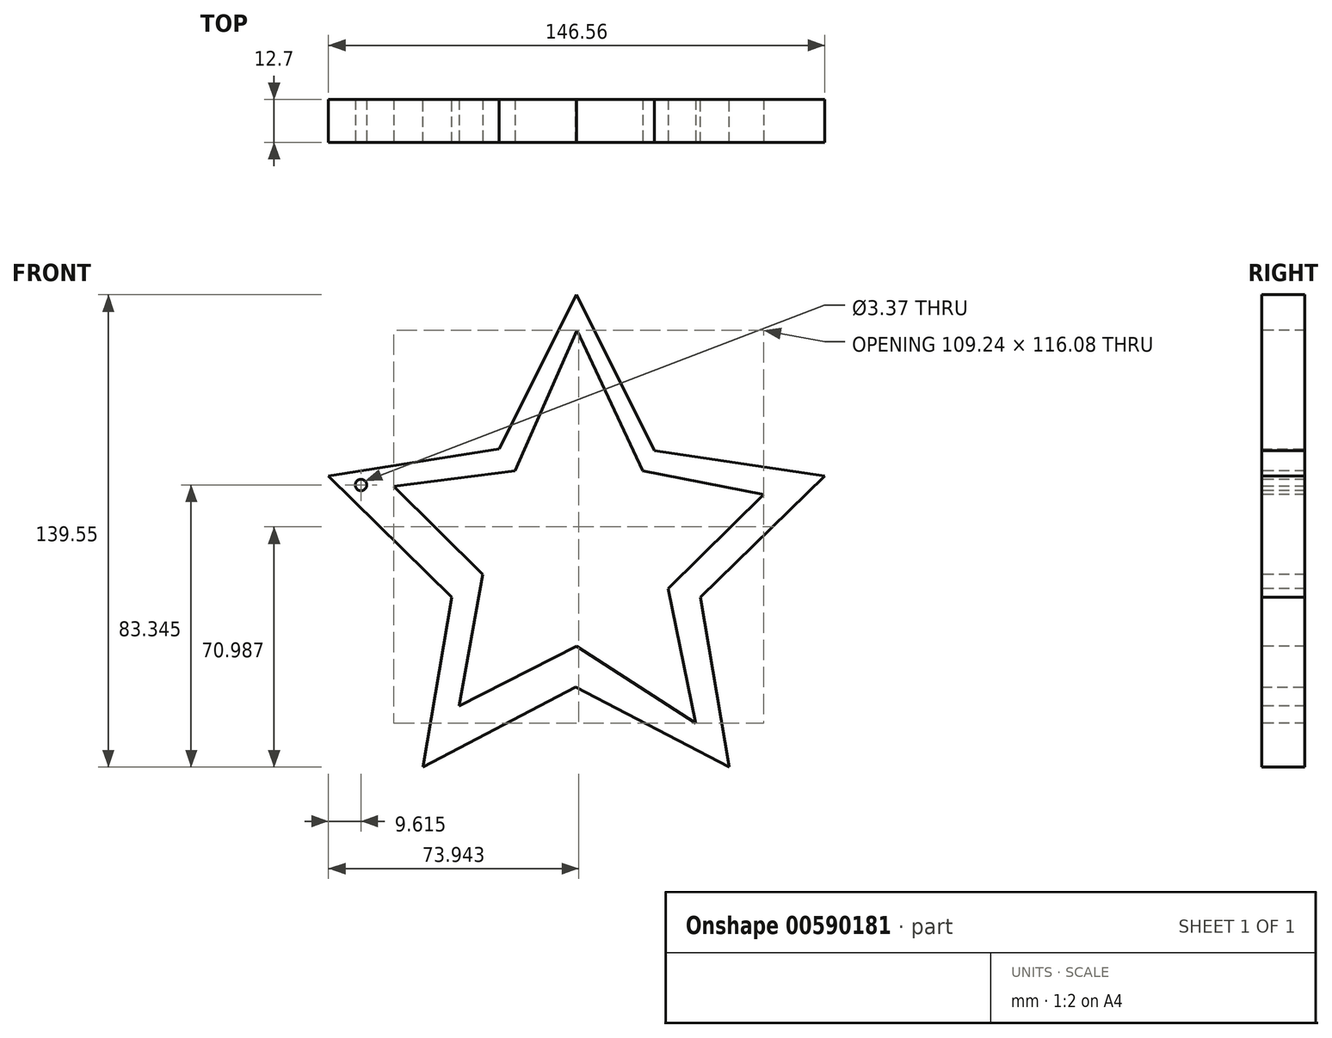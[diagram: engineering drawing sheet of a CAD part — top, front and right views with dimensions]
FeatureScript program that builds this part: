
annotation { "Feature Type Name" : "Feature", "Feature Type Description" : "" }
export const myFeature = defineFeature(function(context is Context, id is Id, definition is map)
    precondition{}
    {
        {
            var Q0;
            Q0=qCreatedBy(makeId("Front.planeOp"),FACE);
            var sketch = newSketch(context, id + "F0", { "sketchPlane" : qUnion([Q0])});
            skLineSegment(sketch, "E0", {"start": v(-16.38, 0) * mm, "end": v(-39.2, -45.54) * mm});
            skLineSegment(sketch, "E1", {"start": v(-39.2, -45.54) * mm, "end": v(-89.66, -53.55) * mm});
            skLineSegment(sketch, "E2", {"start": v(-89.66, -53.55) * mm, "end": v(-53.23, -89.36) * mm});
            skLineSegment(sketch, "E3", {"start": v(-53.23, -89.36) * mm, "end": v(-61.75, -139.55) * mm});
            skLineSegment(sketch, "E4", {"start": v(-61.75, -139.55) * mm, "end": v(-16.67, -115.9) * mm});
            skLineSegment(sketch, "E5", {"start": v(-16.67, -115.9) * mm, "end": v(28.66, -139.55) * mm});
            skLineSegment(sketch, "E6", {"start": v(28.66, -139.55) * mm, "end": v(20.14, -89.36) * mm});
            skLineSegment(sketch, "E7", {"start": v(20.14, -89.36) * mm, "end": v(56.9, -53.55) * mm});
            skLineSegment(sketch, "E8", {"start": v(56.9, -53.55) * mm, "end": v(6.62, -46.04) * mm});
            skLineSegment(sketch, "E9", {"start": v(6.62, -46.04) * mm, "end": v(-16.38, 0) * mm});
            skSolve(sketch);
        }
        {
            var Q0;
            Q0=qSketchRegion(id+"F0",true);
            extrude(context, id + "F1", {"entities" : qUnion([Q0]), "depth" : 12.7 * mm, "offsetDistance" : 25.4 * mm});
        }
        {
            var Q0;
            Q0=makeQuery(id+"F1.opExtrude","CAP_FACE",FACE,{"disambiguationData":[OSD([sQuery(id+"F0.wireOp",EDGE,"E0"),sQuery(id+"F0.wireOp",EDGE,"E1"),sQuery(id+"F0.wireOp",EDGE,"E2"),sQuery(id+"F0.wireOp",EDGE,"E3"),sQuery(id+"F0.wireOp",EDGE,"E4"),sQuery(id+"F0.wireOp",EDGE,"E5"),sQuery(id+"F0.wireOp",EDGE,"E6"),sQuery(id+"F0.wireOp",EDGE,"E7"),sQuery(id+"F0.wireOp",EDGE,"E8"),sQuery(id+"F0.wireOp",EDGE,"E9")])],"isStart":false});
            var sketch = newSketch(context, id + "F2", { "sketchPlane" : qUnion([Q0])});
            skLineSegment(sketch, "E10", {"start": v(-16.27, -10.52) * mm, "end": v(-34.59, -52.01) * mm});
            skLineSegment(sketch, "E11", {"start": v(-34.59, -52.01) * mm, "end": v(-70.34, -56.65) * mm});
            skLineSegment(sketch, "E12", {"start": v(-70.34, -56.65) * mm, "end": v(-44.07, -82.69) * mm});
            skLineSegment(sketch, "E13", {"start": v(-44.07, -82.69) * mm, "end": v(-51.14, -121.53) * mm});
            skLineSegment(sketch, "E14", {"start": v(-51.14, -121.53) * mm, "end": v(-16.38, -103.87) * mm});
            skLineSegment(sketch, "E15", {"start": v(-16.38, -103.87) * mm, "end": v(18.82, -126.6) * mm});
            skLineSegment(sketch, "E16", {"start": v(18.82, -126.6) * mm, "end": v(10.65, -86.88) * mm});
            skLineSegment(sketch, "E17", {"start": v(10.65, -86.88) * mm, "end": v(38.9, -59.07) * mm});
            skLineSegment(sketch, "E18", {"start": v(38.9, -59.07) * mm, "end": v(3.15, -52.01) * mm});
            skLineSegment(sketch, "E19", {"start": v(3.15, -52.01) * mm, "end": v(-16.27, -10.52) * mm});
            skSolve(sketch);
        }
        {
            var Q0;
            Q0=qSketchRegion(id+"F2",true);
            extrude(context, id + "F3", {"entities" : qUnion([Q0]), "operationType" : NewBodyOperationType.REMOVE, "oppositeDirection" : true, "depth" : 25.4 * mm, "offsetDistance" : 25.4 * mm});
        }
        {
            var Q0;
            Q0=makeQuery(id+"F1.opExtrude","CAP_FACE",FACE,{"disambiguationData":[OSD([sQuery(id+"F0.wireOp",EDGE,"E0"),sQuery(id+"F0.wireOp",EDGE,"E1"),sQuery(id+"F0.wireOp",EDGE,"E2"),sQuery(id+"F0.wireOp",EDGE,"E3"),sQuery(id+"F0.wireOp",EDGE,"E4"),sQuery(id+"F0.wireOp",EDGE,"E5"),sQuery(id+"F0.wireOp",EDGE,"E6"),sQuery(id+"F0.wireOp",EDGE,"E7"),sQuery(id+"F0.wireOp",EDGE,"E8"),sQuery(id+"F0.wireOp",EDGE,"E9")])],"isStart":false});
            var sketch = newSketch(context, id + "F4", { "sketchPlane" : qUnion([Q0])});
            skCircle(sketch, "E20", {"center": v(-80.05, -56.2) * mm, "radius": 1.69 * mm});
            skSolve(sketch);
        }
        {
            var Q0;
            Q0=qSketchRegion(id+"F4",true);
            extrude(context, id + "F5", {"entities" : qUnion([Q0]), "operationType" : NewBodyOperationType.REMOVE, "oppositeDirection" : true, "depth" : 25.4 * mm, "offsetDistance" : 25.4 * mm});
        }
    });
